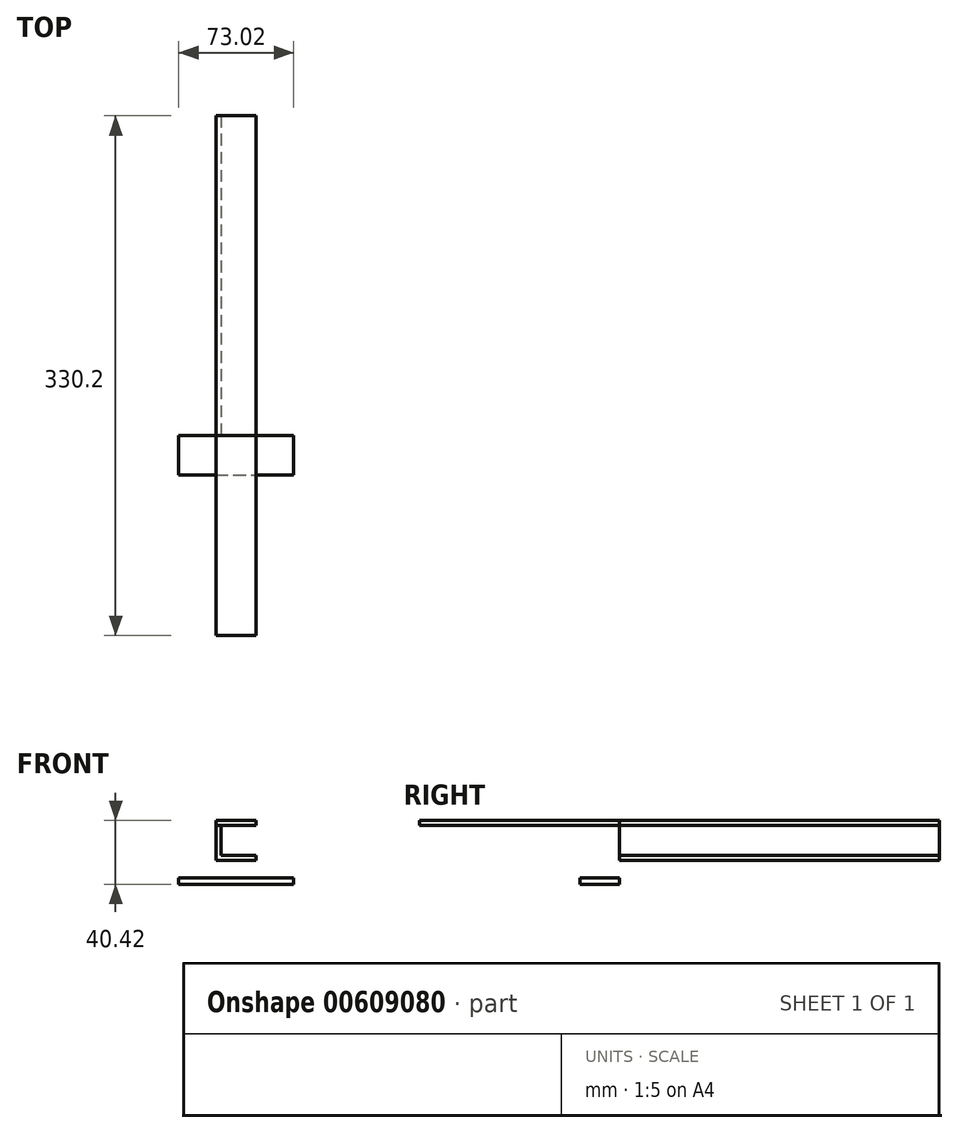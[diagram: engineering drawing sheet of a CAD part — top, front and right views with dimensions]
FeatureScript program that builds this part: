
annotation { "Feature Type Name" : "Feature", "Feature Type Description" : "" }
export const myFeature = defineFeature(function(context is Context, id is Id, definition is map)
    precondition{}
    {
        {
            var Q0;
            Q0=qCreatedBy(makeId("Front.planeOp"),FACE);
            var sketch = newSketch(context, id + "F0", { "sketchPlane" : qUnion([Q0])});
            skLineSegment(sketch, "E0.bottom", {"start": v(-12.7, 12.7) * mm, "end": v(12.7, 12.7) * mm});
            skLineSegment(sketch, "E0.top", {"start": v(-12.7, -12.7) * mm, "end": v(12.7, -12.7) * mm});
            skLineSegment(sketch, "E0.left", {"start": v(-12.7, 12.7) * mm, "end": v(-12.7, -12.7) * mm});
            skLineSegment(sketch, "E0.right", {"start": v(12.7, 12.7) * mm, "end": v(12.7, -12.7) * mm});
            skPoint(sketch, "E0.middle", {"position": v(0, 0) * mm});
            skLineSegment(sketch, "E1", {"start": v(-12.7, -9.53) * mm, "end": v(12.7, -9.53) * mm});
            skLineSegment(sketch, "E2", {"start": v(-12.7, 9.52) * mm, "end": v(12.7, 9.53) * mm});
            skLineSegment(sketch, "E3", {"start": v(-9.52, 9.52) * mm, "end": v(-9.52, -9.53) * mm});
            skSolve(sketch);
        }
        {
            var Q0;
            {var subQ1=sQuery(id+"F0.wireOp",EDGE,"E0.bottom");Q0=makeQuery(id+"F0.imprint","IMPRINT",FACE,{"disambiguationData":[TD([[makeQuery(id+"F0.imprint","IMPRINT",EDGE,{"derivedFrom":subQ1}),-1.0]])]});}
            var Q1;
            {var subQ5=sQuery(id+"F0.wireOp",EDGE,"E3");Q1=makeQuery(id+"F0.imprint","IMPRINT",FACE,{"disambiguationData":[TD([[makeQuery(id+"F0.imprint","IMPRINT",EDGE,{"derivedFrom":subQ5}),-1.0]])]});}
            var Q2;
            {var subQ5=sQuery(id+"F0.wireOp",EDGE,"E0.top");Q2=makeQuery(id+"F0.imprint","IMPRINT",FACE,{"disambiguationData":[TD([[makeQuery(id+"F0.imprint","IMPRINT",EDGE,{"derivedFrom":subQ5}),1.0]])]});}
            extrude(context, id + "F1", {"entities" : qUnion([Q0, Q1, Q2]), "oppositeDirection" : true, "depth" : 203.2 * mm, "offsetDistance" : 25 * mm});
        }
        {
            var Q0;
            {var subQ1=sQuery(id+"F0.wireOp",EDGE,"E0.bottom");Q0=makeQuery(id+"F0.imprint","IMPRINT",FACE,{"disambiguationData":[TD([[makeQuery(id+"F0.imprint","IMPRINT",EDGE,{"derivedFrom":subQ1}),-1.0]])]});}
            extrude(context, id + "F2", {"entities" : qUnion([Q0]), "depth" : 127 * mm, "offsetDistance" : 25 * mm});
        }
        {
            var Q0;
            Q0=qCreatedBy(makeId("Front.planeOp"),FACE);
            var sketch = newSketch(context, id + "F3", { "sketchPlane" : qUnion([Q0])});
            skLineSegment(sketch, "E4.bottom", {"start": v(-36.51, -27.72) * mm, "end": v(36.51, -27.72) * mm});
            skLineSegment(sketch, "E4.top", {"start": v(-36.51, -23.8) * mm, "end": v(36.51, -23.8) * mm});
            skLineSegment(sketch, "E4.left", {"start": v(-36.51, -27.72) * mm, "end": v(-36.51, -23.8) * mm});
            skLineSegment(sketch, "E4.right", {"start": v(36.51, -27.72) * mm, "end": v(36.51, -23.8) * mm});
            skPoint(sketch, "E4.middle", {"position": v(0, -25.76) * mm});
            skSolve(sketch);
        }
        {
            var Q0;
            Q0=makeQuery(id+"F3.imprint","IMPRINT",FACE,{"disambiguationData":[TD([[makeQuery(id+"F3.imprint","IMPRINT",EDGE,{"derivedFrom":sQuery(id+"F3.wireOp",EDGE,"E4.bottom")}),1.0]])]});
            extrude(context, id + "F4", {"entities" : qUnion([Q0]), "depth" : 25 * mm, "offsetDistance" : 25 * mm});
        }
    });
